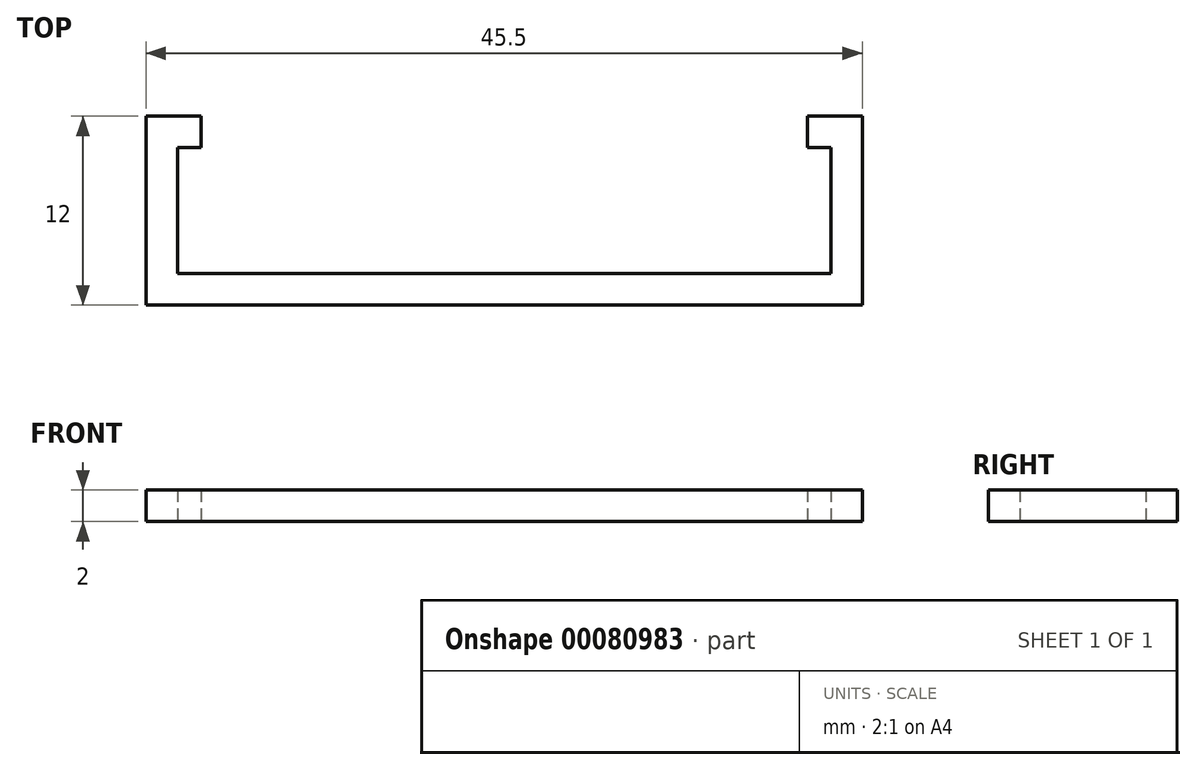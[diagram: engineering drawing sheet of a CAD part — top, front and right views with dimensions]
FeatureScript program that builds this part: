
annotation { "Feature Type Name" : "Feature", "Feature Type Description" : "" }
export const myFeature = defineFeature(function(context is Context, id is Id, definition is map)
    precondition{}
    {
        {
            var Q0;
            Q0=qCreatedBy(makeId("Top.planeOp"),FACE);
            var sketch = newSketch(context, id + "F0", { "sketchPlane" : qUnion([Q0])});
            skLineSegment(sketch, "E0.bottom", {"start": v(-20.45, 0) * mm, "end": v(25.05, 0) * mm});
            skLineSegment(sketch, "E0.top", {"start": v(-20.45, -2) * mm, "end": v(25.05, -2) * mm});
            skLineSegment(sketch, "E0.left", {"start": v(-20.45, 0) * mm, "end": v(-20.45, -2) * mm});
            skLineSegment(sketch, "E0.right", {"start": v(25.05, 0) * mm, "end": v(25.05, -2) * mm});
            skLineSegment(sketch, "E1.bottom", {"start": v(-20.45, -2) * mm, "end": v(-18.45, -2) * mm});
            skLineSegment(sketch, "E1.top", {"start": v(-20.45, 10) * mm, "end": v(-18.45, 10) * mm});
            skLineSegment(sketch, "E1.left", {"start": v(-20.45, -2) * mm, "end": v(-20.45, 10) * mm});
            skLineSegment(sketch, "E1.right", {"start": v(-18.45, -2) * mm, "end": v(-18.45, 10) * mm});
            skLineSegment(sketch, "E2.bottom", {"start": v(25.05, -2) * mm, "end": v(23.05, -2) * mm});
            skLineSegment(sketch, "E2.top", {"start": v(25.05, 10) * mm, "end": v(23.05, 10) * mm});
            skLineSegment(sketch, "E2.left", {"start": v(25.05, -2) * mm, "end": v(25.05, 10) * mm});
            skLineSegment(sketch, "E2.right", {"start": v(23.05, -2) * mm, "end": v(23.05, 10) * mm});
            skLineSegment(sketch, "E3.bottom", {"start": v(25.05, 10) * mm, "end": v(21.55, 10) * mm});
            skLineSegment(sketch, "E3.top", {"start": v(25.05, 8) * mm, "end": v(21.55, 8) * mm});
            skLineSegment(sketch, "E3.left", {"start": v(25.05, 10) * mm, "end": v(25.05, 8) * mm});
            skLineSegment(sketch, "E3.right", {"start": v(21.55, 10) * mm, "end": v(21.55, 8) * mm});
            skLineSegment(sketch, "E4.bottom", {"start": v(-20.45, 10) * mm, "end": v(-16.95, 10) * mm});
            skLineSegment(sketch, "E4.top", {"start": v(-20.45, 8) * mm, "end": v(-16.95, 8) * mm});
            skLineSegment(sketch, "E4.left", {"start": v(-20.45, 10) * mm, "end": v(-20.45, 8) * mm});
            skLineSegment(sketch, "E4.right", {"start": v(-16.95, 10) * mm, "end": v(-16.95, 8) * mm});
            skLineSegment(sketch, "E5", {"start": v(-18.45, 0) * mm, "end": v(-18.45, 8) * mm});
            skLineSegment(sketch, "E6", {"start": v(-20.45, -2) * mm, "end": v(-20.45, 0) * mm});
            skLineSegment(sketch, "E7", {"start": v(-18.45, -2) * mm, "end": v(-18.45, 0) * mm});
            skLineSegment(sketch, "E8", {"start": v(23.05, 0) * mm, "end": v(23.05, 8) * mm});
            skLineSegment(sketch, "E9", {"start": v(-18.45, 0) * mm, "end": v(23.05, 0) * mm});
            skLineSegment(sketch, "E10", {"start": v(-18.45, -2) * mm, "end": v(23.05, -2) * mm});
            skSolve(sketch);
        }
        {
            var Q0;
            Q0 = qSketchRegion(id + "F0", true);
            extrude(context, id + "F1", {"entities" : qUnion([Q0]), "depth" : 2 * mm});
        }
    });
